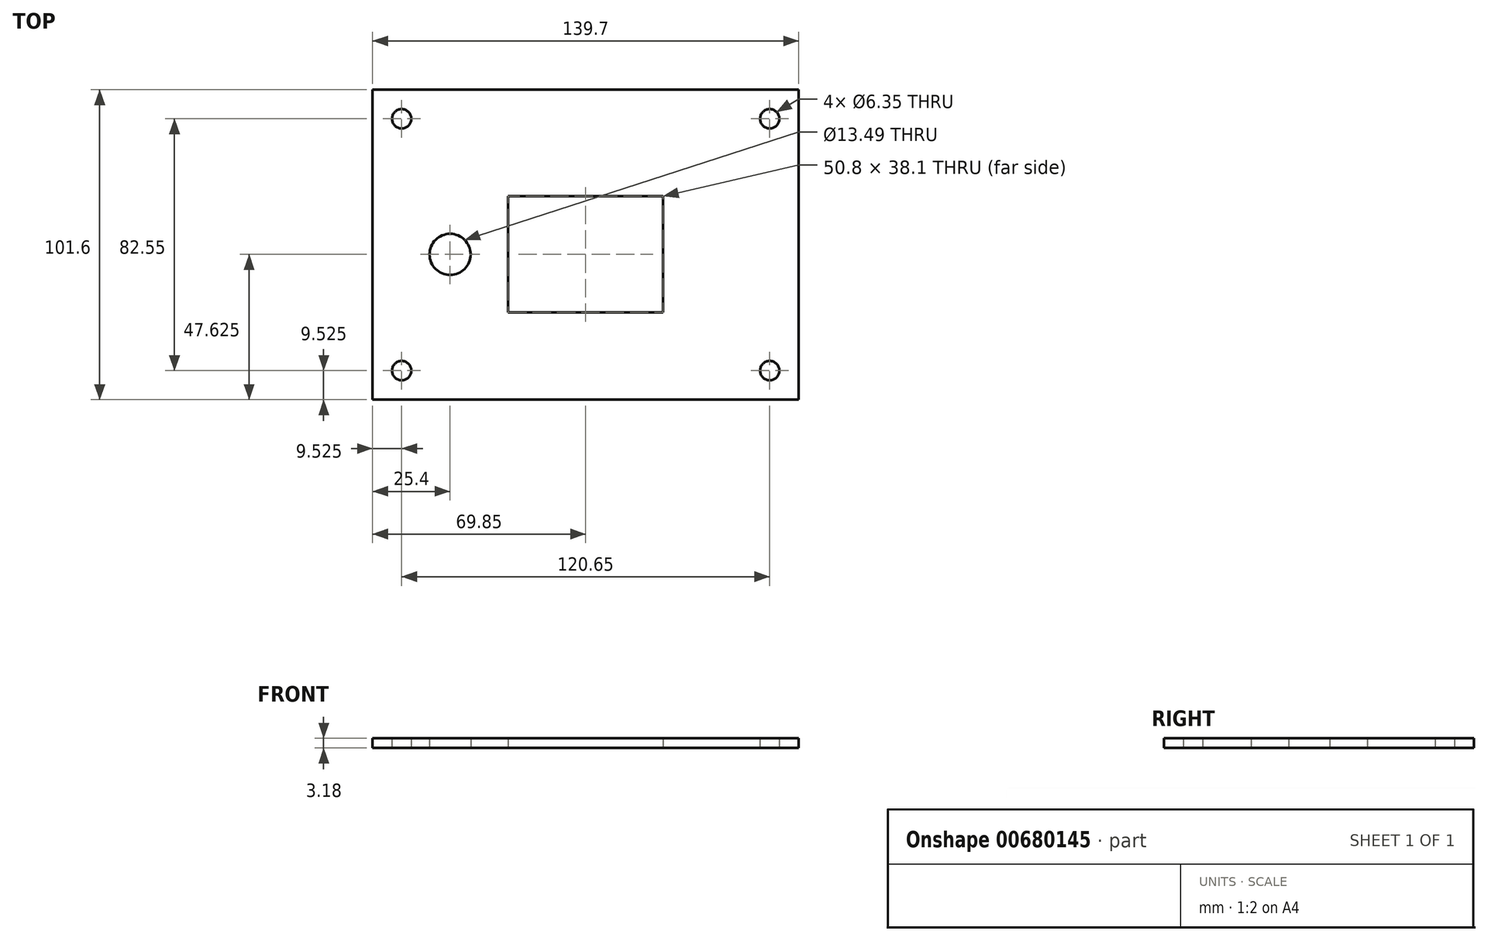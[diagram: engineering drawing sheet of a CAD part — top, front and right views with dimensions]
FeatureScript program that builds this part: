
annotation { "Feature Type Name" : "Feature", "Feature Type Description" : "" }
export const myFeature = defineFeature(function(context is Context, id is Id, definition is map)
    precondition{}
    {
        {
            var Q0;
            Q0=qCreatedBy(makeId("Top.planeOp"),FACE);
            var sketch = newSketch(context, id + "F0", { "sketchPlane" : qUnion([Q0])});
            skLineSegment(sketch, "E0.bottom", {"start": v(0, 0) * mm, "end": v(139.7, 0) * mm});
            skLineSegment(sketch, "E0.top", {"start": v(0, 101.6) * mm, "end": v(139.7, 101.6) * mm});
            skLineSegment(sketch, "E0.left", {"start": v(0, 0) * mm, "end": v(0, 101.6) * mm});
            skLineSegment(sketch, "E0.right", {"start": v(139.7, 0) * mm, "end": v(139.7, 101.6) * mm});
            skCircle(sketch, "E1", {"center": v(130.18, 92.08) * mm, "radius": 3.18 * mm});
            skCircle(sketch, "E2", {"center": v(9.53, 92.08) * mm, "radius": 3.18 * mm});
            skCircle(sketch, "E3", {"center": v(9.53, 9.52) * mm, "radius": 3.18 * mm});
            skCircle(sketch, "E4", {"center": v(130.18, 9.53) * mm, "radius": 3.18 * mm});
            skLineSegment(sketch, "E5.bottom", {"start": v(44.45, 66.67) * mm, "end": v(95.25, 66.67) * mm});
            skLineSegment(sketch, "E5.top", {"start": v(44.45, 28.58) * mm, "end": v(95.25, 28.58) * mm});
            skLineSegment(sketch, "E5.left", {"start": v(44.45, 66.67) * mm, "end": v(44.45, 28.58) * mm});
            skLineSegment(sketch, "E5.right", {"start": v(95.25, 66.67) * mm, "end": v(95.25, 28.58) * mm});
            skCircle(sketch, "E6", {"center": v(25.4, 47.62) * mm, "radius": 6.75 * mm});
            skSolve(sketch);
        }
        {
            var Q0;
            Q0=makeQuery(id+"F0.imprint","IMPRINT",FACE,{"disambiguationData":[TD([[makeQuery(id+"F0.imprint","IMPRINT",EDGE,{"derivedFrom":sQuery(id+"F0.wireOp",EDGE,"E0.bottom")}),1.0]])]});
            var Q1;
            Q1=makeQuery(id+"F0.imprint","IMPRINT",FACE,{"disambiguationData":[TD([[makeQuery(id+"F0.imprint","IMPRINT",EDGE,{"derivedFrom":sQuery(id+"F0.wireOp",EDGE,"qlQYrncj-8nrb-7wBW-jvim-BRO9nLefTFWl")}),-1.0]])]});
            var Q2;
            Q2=makeQuery(id+"F0.imprint","IMPRINT",FACE,{"disambiguationData":[TD([[makeQuery(id+"F0.imprint","IMPRINT",EDGE,{"derivedFrom":sQuery(id+"F0.wireOp",EDGE,"34f1016c-1b43-47f8-b070-84d3ffa842ec.1.0.0")}),1.0]])]});
            var Q3;
            Q3=makeQuery(id+"F0.imprint","IMPRINT",FACE,{"disambiguationData":[TD([[makeQuery(id+"F0.imprint","IMPRINT",EDGE,{"derivedFrom":sQuery(id+"F0.wireOp",EDGE,"34f1016c-1b43-47f8-b070-84d3ffa842ec.2.0.0")}),1.0]])]});
            var Q4;
            Q4=makeQuery(id+"F0.imprint","IMPRINT",FACE,{"disambiguationData":[TD([[makeQuery(id+"F0.imprint","IMPRINT",EDGE,{"derivedFrom":sQuery(id+"F0.wireOp",EDGE,"34f1016c-1b43-47f8-b070-84d3ffa842ec.2.1.0")}),1.0]])]});
            var Q5;
            Q5=makeQuery(id+"F0.imprint","IMPRINT",FACE,{"disambiguationData":[TD([[makeQuery(id+"F0.imprint","IMPRINT",EDGE,{"derivedFrom":sQuery(id+"F0.wireOp",EDGE,"34f1016c-1b43-47f8-b070-84d3ffa842ec.1.1.0")}),1.0]])]});
            var Q6;
            Q6=makeQuery(id+"F0.imprint","IMPRINT",FACE,{"disambiguationData":[TD([[makeQuery(id+"F0.imprint","IMPRINT",EDGE,{"derivedFrom":sQuery(id+"F0.wireOp",EDGE,"34f1016c-1b43-47f8-b070-84d3ffa842ec.0.1.0")}),1.0]])]});
            extrude(context, id + "F1", {"entities" : qUnion([Q0, Q1, Q2, Q3, Q4, Q5, Q6]), "depth" : 3.17 * mm, "offsetDistance" : 25.4 * mm});
        }
    });
